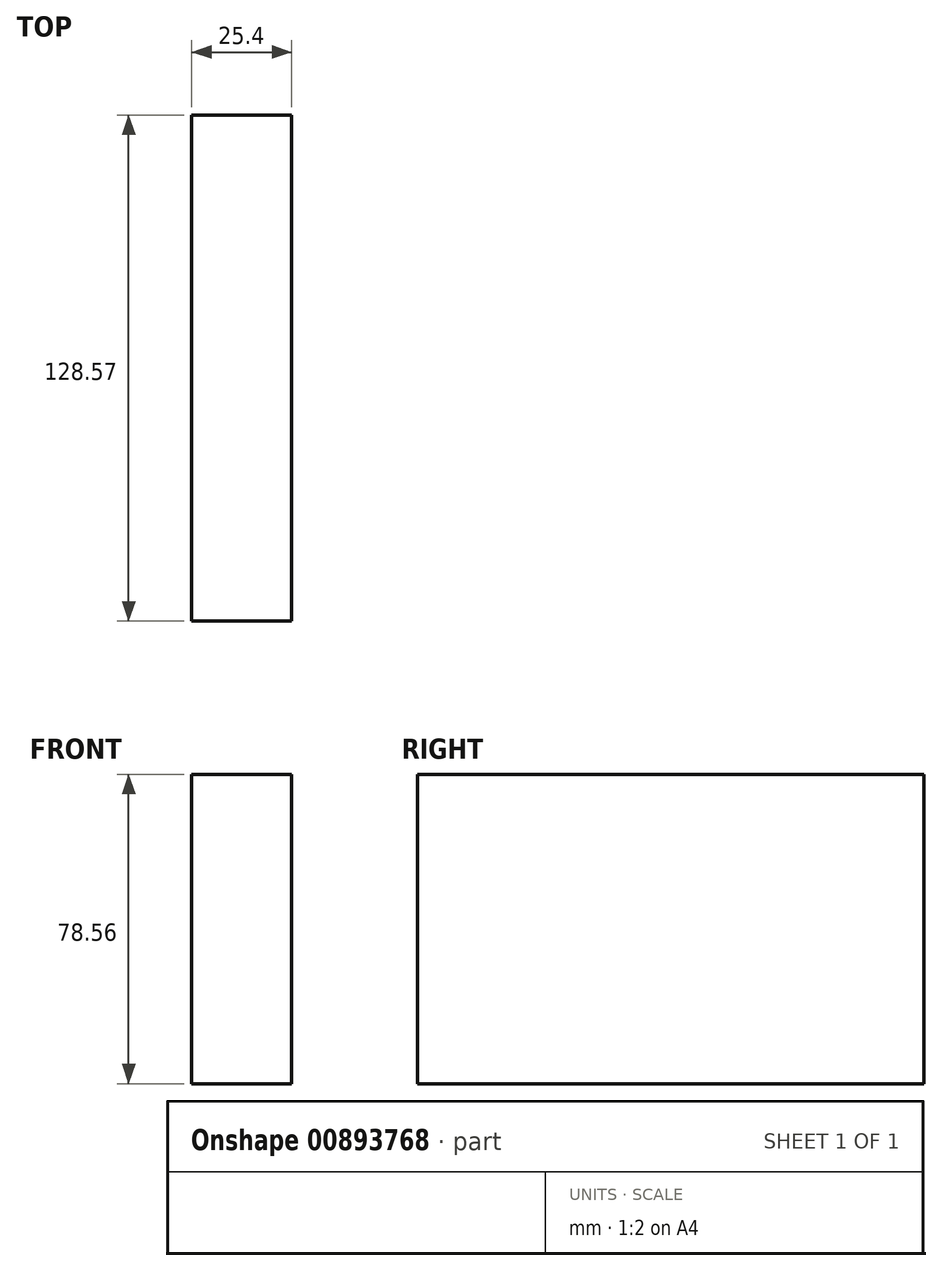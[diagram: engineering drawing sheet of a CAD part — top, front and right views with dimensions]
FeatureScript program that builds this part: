
annotation { "Feature Type Name" : "Feature", "Feature Type Description" : "" }
export const myFeature = defineFeature(function(context is Context, id is Id, definition is map)
    precondition{}
    {
        {
            var Q0;
            Q0=qCreatedBy(makeId("Right.planeOp"),FACE);
            var sketch = newSketch(context, id + "F0", { "sketchPlane" : qUnion([Q0])});
            skLineSegment(sketch, "E0.bottom", {"start": v(-60.06, 30.48) * mm, "end": v(68.51, 30.48) * mm});
            skLineSegment(sketch, "E0.top", {"start": v(-60.06, -48.08) * mm, "end": v(68.51, -48.08) * mm});
            skLineSegment(sketch, "E0.left", {"start": v(-60.06, 30.48) * mm, "end": v(-60.06, -48.08) * mm});
            skLineSegment(sketch, "E0.right", {"start": v(68.51, 30.48) * mm, "end": v(68.51, -48.08) * mm});
            skSolve(sketch);
        }
        {
            var Q0;
            Q0 = qSketchRegion(id + "F0", true);
            extrude(context, id + "F1", {"entities" : qUnion([Q0]), "depth" : 25.4 * mm, "offsetDistance" : 25.4 * mm});
        }
    });
